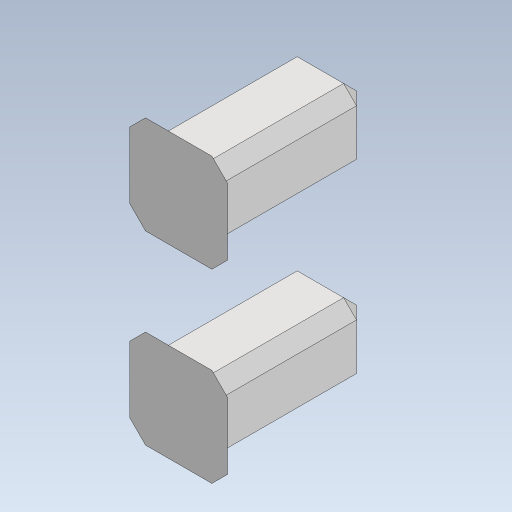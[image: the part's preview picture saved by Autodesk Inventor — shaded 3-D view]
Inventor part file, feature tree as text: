
AUTODESK INVENTOR PART (.ipt)
format: ipt  version: 2023 (Build 270158030, 158C)  size: 158,720 bytes
history: native  units: mm
features: reference x9, other x5, extrude x2, chamfer x2, sketch x2, projected_geometry x2
ambient origin geometry x8: Origin, YZ Plane, XZ Plane, XY Plane, X Axis, Y Axis, Z Axis, Center Point
bodies: Body1 (feature_tree)
feature tree (22):
  other  "V4-pegs"
  extrude  "Extrusion1"  Depth=0.1mm
  extrude  "Extrusion2"  Depth=6.0mm TaperAngle=0.0deg
  chamfer  "Chamfer1"  Distance=0.5mm Angle=45.0deg
  chamfer  "Chamfer2"  Distance=0.5mm Angle=45.0deg
  sketch  "Sketch1"  dims[d0=0.1mm d1=0.1mm]
  reference  "Reference1"
  sketch  "Sketch2"  dims[d2=6.0mm d3=0.0mm d4=0.5mm d5=0.0mm d6=0.5mm d7=2.0mm d8=45.0deg d9=0.5mm d10=2.0mm d11=45.0deg]
  projected_geometry  "Projected Loop1"
  projected_geometry  "Projected Loop2"
  reference  "Reference2"
  reference  "Reference3"
  reference  "Reference4"
  reference  "Reference5"
  reference  "Reference6"
  reference  "Reference7"
  reference  "Reference8"
  reference  "Reference9"
  other  "<userpath>\Documents\0004-inventor\3D-CAD-main\trebuchet\V4.0-trebuchet-printable.iam"
  other  "V4.0-trebuchet-printable.iam"
  other  "V4-baseplate:1"
  other  "v4-latch:1"
